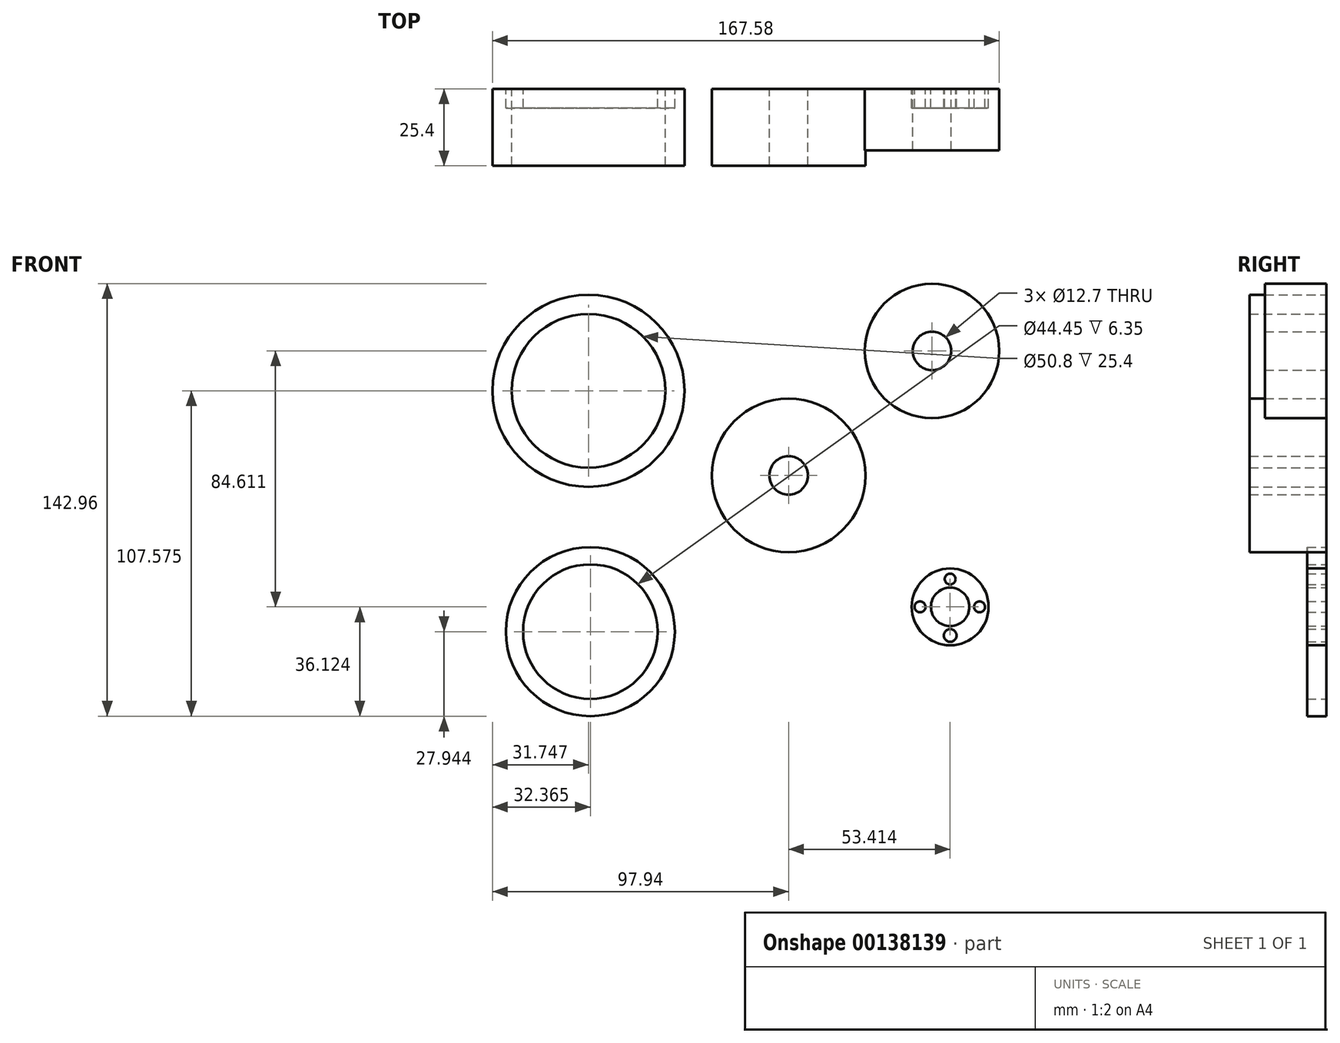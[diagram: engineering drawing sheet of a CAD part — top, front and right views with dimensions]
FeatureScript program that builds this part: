
annotation { "Feature Type Name" : "Feature", "Feature Type Description" : "" }
export const myFeature = defineFeature(function(context is Context, id is Id, definition is map)
    precondition{}
    {
        {
            var Q0;
            Q0=qCreatedBy(makeId("Front.planeOp"),FACE);
            var sketch = newSketch(context, id + "F0", { "sketchPlane" : qUnion([Q0])});
            skCircle(sketch, "E0", {"center": v(0, 0) * mm, "radius": 25.4 * mm});
            skCircle(sketch, "E1", {"center": v(-66.2, 28) * mm, "radius": 25.4 * mm});
            skCircle(sketch, "E2", {"center": v(-66.2, 28) * mm, "radius": 31.75 * mm});
            skCircle(sketch, "E3", {"center": v(0, 0) * mm, "radius": 6.35 * mm});
            skSolve(sketch);
        }
        {
            var Q0;
            Q0 = qSketchRegion(id + "F0", true);
            extrude(context, id + "F1", {"entities" : qUnion([Q0]), "depth" : 25.4 * mm});
        }
        {
            var Q0;
            Q0=qCreatedBy(makeId("Front.planeOp"),FACE);
            var sketch = newSketch(context, id + "F2", { "sketchPlane" : qUnion([Q0])});
            skCircle(sketch, "E4", {"center": v(47.41, 41.16) * mm, "radius": 22.23 * mm});
            skCircle(sketch, "E5", {"center": v(47.41, 41.16) * mm, "radius": 6.35 * mm});
            skSolve(sketch);
        }
        {
            var Q0;
            Q0 = qSketchRegion(id + "F2", true);
            extrude(context, id + "F3", {"entities" : qUnion([Q0]), "depth" : 20.32 * mm});
        }
        {
            var Q0;
            Q0=qCreatedBy(makeId("Front.planeOp"),FACE);
            var sketch = newSketch(context, id + "F4", { "sketchPlane" : qUnion([Q0])});
            skCircle(sketch, "E6", {"center": v(-65.57, -51.64) * mm, "radius": 27.94 * mm});
            skCircle(sketch, "E7", {"center": v(-65.57, -51.64) * mm, "radius": 22.23 * mm});
            skSolve(sketch);
        }
        {
            var Q0;
            Q0 = qSketchRegion(id + "F4", true);
            extrude(context, id + "F5", {"entities" : qUnion([Q0]), "depth" : 6.35 * mm});
        }
        {
            var Q0;
            Q0=qCreatedBy(makeId("Front.planeOp"),FACE);
            var sketch = newSketch(context, id + "F6", { "sketchPlane" : qUnion([Q0])});
            skCircle(sketch, "E8", {"center": v(53.41, -43.46) * mm, "radius": 12.7 * mm});
            skCircle(sketch, "E9", {"center": v(53.41, -43.46) * mm, "radius": 6.35 * mm});
            skCircle(sketch, "E10", {"center": v(53.41, -34.25) * mm, "radius": 1.79 * mm});
            skCircle(sketch, "E11", {"center": v(63.13, -43.46) * mm, "radius": 1.8 * mm});
            skCircle(sketch, "E12", {"center": v(53.41, -52.91) * mm, "radius": 2.1 * mm});
            skCircle(sketch, "E13", {"center": v(43.44, -43.46) * mm, "radius": 1.8 * mm});
            skSolve(sketch);
        }
        {
            var Q0;
            Q0 = qSketchRegion(id + "F6", true);
            extrude(context, id + "F7", {"entities" : qUnion([Q0]), "depth" : 6.35 * mm});
        }
    });
